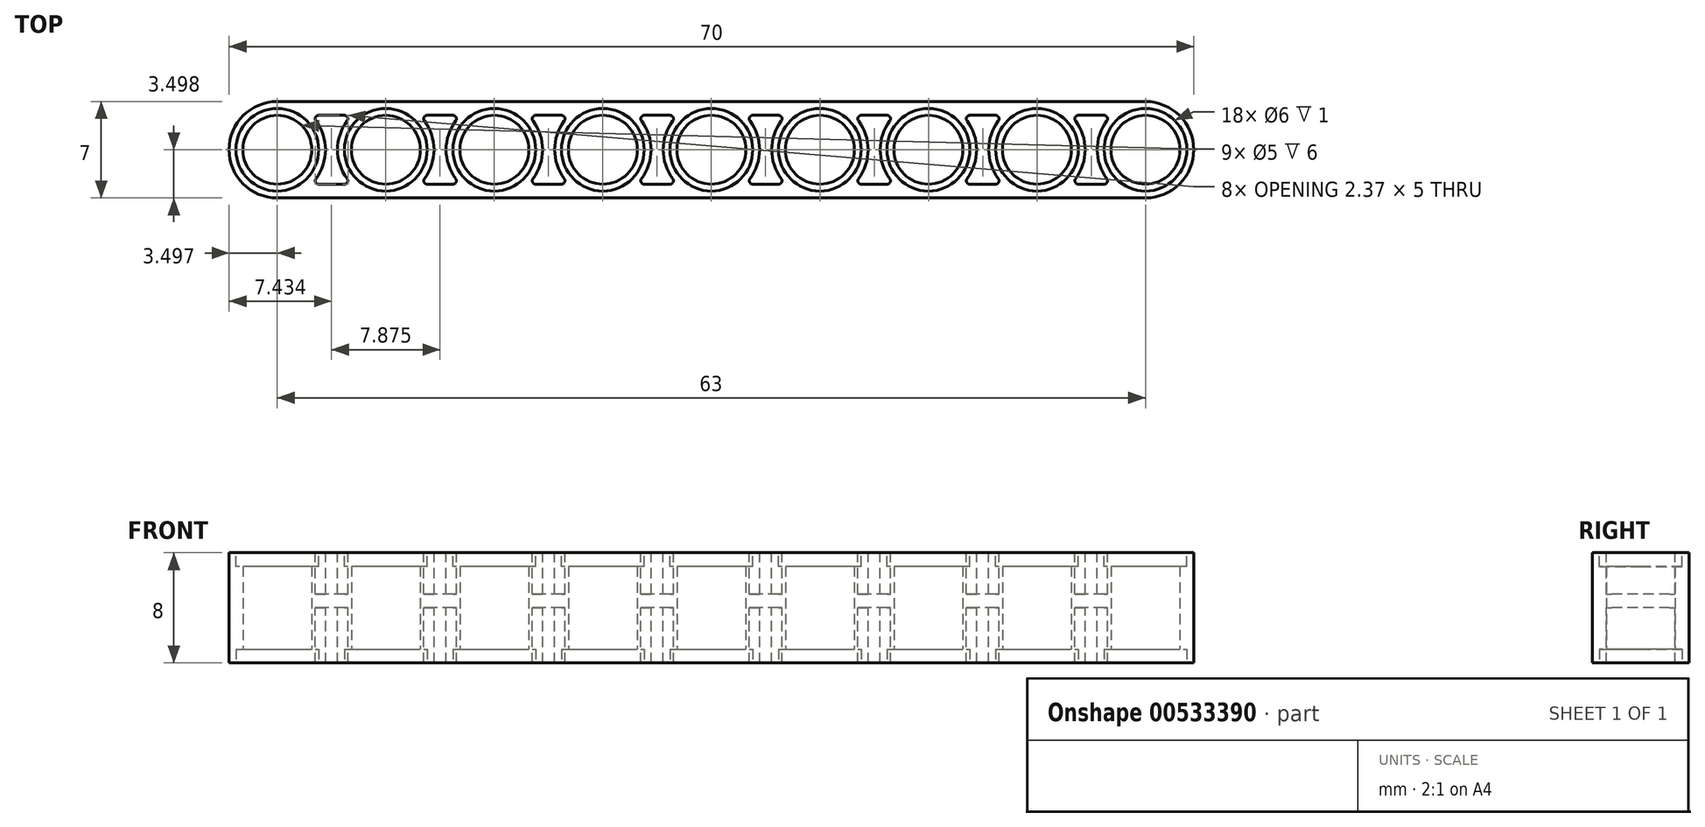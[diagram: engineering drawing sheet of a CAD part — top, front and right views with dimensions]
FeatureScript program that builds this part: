
annotation { "Feature Type Name" : "Feature", "Feature Type Description" : "" }
export const myFeature = defineFeature(function(context is Context, id is Id, definition is map)
    precondition{}
    {
        {
            var Q0;
            Q0=qCreatedBy(makeId("Top.planeOp"),FACE);
            var sketch = newSketch(context, id + "F0", { "sketchPlane" : qUnion([Q0])});
            skCircle(sketch, "E0", {"center": v(-40.67, -41.82) * mm, "radius": 3.5 * mm});
            skLineSegment(sketch, "E1", {"start": v(-40.67, -41.82) * mm, "end": v(22.33, -41.82) * mm});
            skCircle(sketch, "E2", {"center": v(22.33, -41.82) * mm, "radius": 3.5 * mm});
            skLineSegment(sketch, "E3", {"start": v(22.33, -45.32) * mm, "end": v(-40.67, -45.32) * mm});
            skLineSegment(sketch, "E4", {"start": v(-40.67, -38.32) * mm, "end": v(22.33, -38.32) * mm});
            skSolve(sketch);
        }
        {
            var Q0;
            Q0 = qSketchRegion(id + "F0", true);
            extrude(context, id + "F1", {"entities" : qUnion([Q0]), "depth" : 8 * mm, "offsetDistance" : 25 * mm});
        }
        {
            var Q0;
            Q0=makeQuery(id+"F1.opExtrude","CAP_FACE",FACE,{"disambiguationData":[OSD([sQuery(id+"F0.wireOp",EDGE,"E0"),sQuery(id+"F0.wireOp",EDGE,"E2"),sQuery(id+"F0.wireOp",EDGE,"E3"),sQuery(id+"F0.wireOp",EDGE,"E4")])],"isStart":true});
            var sketch = newSketch(context, id + "F2", { "sketchPlane" : qUnion([Q0])});
            skArc(sketch, "E5.0", {"start": v(-40.71, -42.4) * mm, "mid": v(-38.21, -39.9) * mm, "end": v(-40.71, -37.4) * mm});
            skArc(sketch, "E5.1", {"start": v(-40.71, -37.4) * mm, "mid": v(-43.21, -39.9) * mm, "end": v(-40.71, -42.4) * mm});
            skCircle(sketch, "E6.0", {"center": v(-40.71, -39.9) * mm, "radius": 3 * mm});
            skLineSegment(sketch, "E7", {"start": v(-38.26, -42.4) * mm, "end": v(-35.16, -42.4) * mm});
            skLineSegment(sketch, "E8", {"start": v(-38.26, -37.4) * mm, "end": v(-35.16, -37.4) * mm});
            skArc(sketch, "E9", {"start": v(-35.16, -37.4) * mm, "mid": v(-36.21, -39.9) * mm, "end": v(-35.16, -42.4) * mm});
            skArc(sketch, "E10", {"start": v(-38.26, -42.4) * mm, "mid": v(-37.21, -39.9) * mm, "end": v(-38.26, -37.4) * mm});
            skCircle(sketch, "E11", {"center": v(-40.67, 41.82) * mm, "radius": 3 * mm});
            skCircle(sketch, "E12", {"center": v(-40.67, 41.82) * mm, "radius": 2.5 * mm});
            skCircle(sketch, "E13.1.0.0", {"center": v(-32.8, 41.82) * mm, "radius": 2.5 * mm});
            skCircle(sketch, "E13.1.0.1", {"center": v(-32.8, 41.82) * mm, "radius": 3 * mm});
            skCircle(sketch, "E13.2.0.0", {"center": v(-24.92, 41.82) * mm, "radius": 2.5 * mm});
            skCircle(sketch, "E13.2.0.1", {"center": v(-24.92, 41.82) * mm, "radius": 3 * mm});
            skCircle(sketch, "E13.3.0.0", {"center": v(-17.05, 41.82) * mm, "radius": 2.5 * mm});
            skCircle(sketch, "E13.3.0.1", {"center": v(-17.05, 41.82) * mm, "radius": 3 * mm});
            skCircle(sketch, "E13.4.0.0", {"center": v(-9.17, 41.82) * mm, "radius": 2.5 * mm});
            skCircle(sketch, "E13.4.0.1", {"center": v(-9.17, 41.82) * mm, "radius": 3 * mm});
            skCircle(sketch, "E13.5.0.0", {"center": v(-1.3, 41.82) * mm, "radius": 2.5 * mm});
            skCircle(sketch, "E13.5.0.1", {"center": v(-1.3, 41.82) * mm, "radius": 3 * mm});
            skCircle(sketch, "E13.6.0.0", {"center": v(6.58, 41.82) * mm, "radius": 2.5 * mm});
            skCircle(sketch, "E13.6.0.1", {"center": v(6.58, 41.82) * mm, "radius": 3 * mm});
            skCircle(sketch, "E13.7.0.0", {"center": v(14.45, 41.82) * mm, "radius": 2.5 * mm});
            skCircle(sketch, "E13.7.0.1", {"center": v(14.45, 41.82) * mm, "radius": 3 * mm});
            skCircle(sketch, "E13.8.0.0", {"center": v(22.33, 41.82) * mm, "radius": 2.5 * mm});
            skCircle(sketch, "E13.8.0.1", {"center": v(22.33, 41.82) * mm, "radius": 3 * mm});
            skLineSegment(sketch, "E13.direction1", {"start": v(-40.67, 41.82) * mm, "end": v(-32.8, 41.82) * mm, "construction": true});
            skSolve(sketch);
        }
        {
            var Q0;
            Q0=makeQuery(id+"F2.imprint","IMPRINT",FACE,{"disambiguationData":[TD([[makeQuery(id+"F2.imprint","IMPRINT",EDGE,{"derivedFrom":sQuery(id+"F2.wireOp",EDGE,"E12")}),1.0]])]});
            var Q1;
            Q1=makeQuery(id+"F2.imprint","IMPRINT",FACE,{"disambiguationData":[TD([[makeQuery(id+"F2.imprint","IMPRINT",EDGE,{"derivedFrom":sQuery(id+"F2.wireOp",EDGE,"E13.1.0.0")}),1.0]])]});
            var Q2;
            Q2=makeQuery(id+"F2.imprint","IMPRINT",FACE,{"disambiguationData":[TD([[makeQuery(id+"F2.imprint","IMPRINT",EDGE,{"derivedFrom":sQuery(id+"F2.wireOp",EDGE,"E13.2.0.0")}),1.0]])]});
            var Q3;
            Q3=makeQuery(id+"F2.imprint","IMPRINT",FACE,{"disambiguationData":[TD([[makeQuery(id+"F2.imprint","IMPRINT",EDGE,{"derivedFrom":sQuery(id+"F2.wireOp",EDGE,"E13.3.0.0")}),1.0]])]});
            var Q4;
            Q4=makeQuery(id+"F2.imprint","IMPRINT",FACE,{"disambiguationData":[TD([[makeQuery(id+"F2.imprint","IMPRINT",EDGE,{"derivedFrom":sQuery(id+"F2.wireOp",EDGE,"E13.4.0.0")}),1.0]])]});
            var Q5;
            Q5=makeQuery(id+"F2.imprint","IMPRINT",FACE,{"disambiguationData":[TD([[makeQuery(id+"F2.imprint","IMPRINT",EDGE,{"derivedFrom":sQuery(id+"F2.wireOp",EDGE,"E13.5.0.0")}),1.0]])]});
            var Q6;
            Q6=makeQuery(id+"F2.imprint","IMPRINT",FACE,{"disambiguationData":[TD([[makeQuery(id+"F2.imprint","IMPRINT",EDGE,{"derivedFrom":sQuery(id+"F2.wireOp",EDGE,"E13.6.0.0")}),1.0]])]});
            var Q7;
            Q7=makeQuery(id+"F2.imprint","IMPRINT",FACE,{"disambiguationData":[TD([[makeQuery(id+"F2.imprint","IMPRINT",EDGE,{"derivedFrom":sQuery(id+"F2.wireOp",EDGE,"E13.7.0.0")}),1.0]])]});
            var Q8;
            Q8=makeQuery(id+"F2.imprint","IMPRINT",FACE,{"disambiguationData":[TD([[makeQuery(id+"F2.imprint","IMPRINT",EDGE,{"derivedFrom":sQuery(id+"F2.wireOp",EDGE,"E13.8.0.0")}),1.0]])]});
            extrude(context, id + "F3", {"entities" : qUnion([Q0, Q1, Q2, Q3, Q4, Q5, Q6, Q7, Q8]), "operationType" : NewBodyOperationType.REMOVE, "oppositeDirection" : true, "depth" : 25 * mm, "offsetDistance" : 25 * mm});
        }
        {
            var Q0;
            Q0=makeQuery(id+"F2.imprint","IMPRINT",FACE,{"disambiguationData":[TD([[makeQuery(id+"F2.imprint","IMPRINT",EDGE,{"derivedFrom":sQuery(id+"F2.wireOp",EDGE,"E11")}),1.0]])]});
            var Q1;
            Q1=makeQuery(id+"F2.imprint","IMPRINT",FACE,{"disambiguationData":[TD([[makeQuery(id+"F2.imprint","IMPRINT",EDGE,{"derivedFrom":sQuery(id+"F2.wireOp",EDGE,"E13.1.0.0")}),-1.0]])]});
            var Q2;
            Q2=makeQuery(id+"F2.imprint","IMPRINT",FACE,{"disambiguationData":[TD([[makeQuery(id+"F2.imprint","IMPRINT",EDGE,{"derivedFrom":sQuery(id+"F2.wireOp",EDGE,"E13.2.0.0")}),-1.0]])]});
            var Q3;
            Q3=makeQuery(id+"F2.imprint","IMPRINT",FACE,{"disambiguationData":[TD([[makeQuery(id+"F2.imprint","IMPRINT",EDGE,{"derivedFrom":sQuery(id+"F2.wireOp",EDGE,"E13.3.0.0")}),-1.0]])]});
            var Q4;
            Q4=makeQuery(id+"F2.imprint","IMPRINT",FACE,{"disambiguationData":[TD([[makeQuery(id+"F2.imprint","IMPRINT",EDGE,{"derivedFrom":sQuery(id+"F2.wireOp",EDGE,"E13.4.0.0")}),-1.0]])]});
            var Q5;
            Q5=makeQuery(id+"F2.imprint","IMPRINT",FACE,{"disambiguationData":[TD([[makeQuery(id+"F2.imprint","IMPRINT",EDGE,{"derivedFrom":sQuery(id+"F2.wireOp",EDGE,"E13.5.0.0")}),-1.0]])]});
            var Q6;
            Q6=makeQuery(id+"F2.imprint","IMPRINT",FACE,{"disambiguationData":[TD([[makeQuery(id+"F2.imprint","IMPRINT",EDGE,{"derivedFrom":sQuery(id+"F2.wireOp",EDGE,"E13.6.0.0")}),-1.0]])]});
            var Q7;
            Q7=makeQuery(id+"F2.imprint","IMPRINT",FACE,{"disambiguationData":[TD([[makeQuery(id+"F2.imprint","IMPRINT",EDGE,{"derivedFrom":sQuery(id+"F2.wireOp",EDGE,"E13.7.0.0")}),-1.0]])]});
            var Q8;
            Q8=makeQuery(id+"F2.imprint","IMPRINT",FACE,{"disambiguationData":[TD([[makeQuery(id+"F2.imprint","IMPRINT",EDGE,{"derivedFrom":sQuery(id+"F2.wireOp",EDGE,"E13.8.0.0")}),-1.0]])]});
            extrude(context, id + "F4", {"entities" : qUnion([Q0, Q1, Q2, Q3, Q4, Q5, Q6, Q7, Q8]), "operationType" : NewBodyOperationType.REMOVE, "oppositeDirection" : true, "depth" : 1 * mm, "offsetDistance" : 25 * mm});
        }
        {
            var Q0;
            Q0=makeQuery(id+"F1.opExtrude","CAP_FACE",FACE,{"disambiguationData":[OSD([sQuery(id+"F0.wireOp",EDGE,"E0"),sQuery(id+"F0.wireOp",EDGE,"E2"),sQuery(id+"F0.wireOp",EDGE,"E3"),sQuery(id+"F0.wireOp",EDGE,"E4")])],"isStart":false});
            var sketch = newSketch(context, id + "F5", { "sketchPlane" : qUnion([Q0])});
            skCircle(sketch, "E14", {"center": v(22.33, -41.82) * mm, "radius": 3 * mm});
            skCircle(sketch, "E15.1.0.0", {"center": v(14.45, -41.82) * mm, "radius": 3 * mm});
            skCircle(sketch, "E15.2.0.0", {"center": v(6.58, -41.82) * mm, "radius": 3 * mm});
            skCircle(sketch, "E15.3.0.0", {"center": v(-1.3, -41.82) * mm, "radius": 3 * mm});
            skCircle(sketch, "E15.4.0.0", {"center": v(-9.17, -41.82) * mm, "radius": 3 * mm});
            skCircle(sketch, "E15.5.0.0", {"center": v(-17.05, -41.82) * mm, "radius": 3 * mm});
            skCircle(sketch, "E15.6.0.0", {"center": v(-24.92, -41.82) * mm, "radius": 3 * mm});
            skCircle(sketch, "E15.7.0.0", {"center": v(-32.8, -41.82) * mm, "radius": 3 * mm});
            skCircle(sketch, "E15.8.0.0", {"center": v(-40.67, -41.82) * mm, "radius": 3 * mm});
            skLineSegment(sketch, "E15.direction1", {"start": v(22.33, -41.82) * mm, "end": v(14.45, -41.82) * mm, "construction": true});
            skSolve(sketch);
        }
        {
            var Q0;
            Q0=makeQuery(id+"F5.imprint","IMPRINT",FACE,{"disambiguationData":[TD([[makeQuery(id+"F5.imprint","IMPRINT",EDGE,{"derivedFrom":sQuery(id+"F5.wireOp",EDGE,"E14")}),1.0]])]});
            var Q1;
            Q1=makeQuery(id+"F5.imprint","IMPRINT",FACE,{"disambiguationData":[TD([[makeQuery(id+"F5.imprint","IMPRINT",EDGE,{"derivedFrom":sQuery(id+"F5.wireOp",EDGE,"E15.1.0.0")}),1.0]])]});
            var Q2;
            Q2=makeQuery(id+"F5.imprint","IMPRINT",FACE,{"disambiguationData":[TD([[makeQuery(id+"F5.imprint","IMPRINT",EDGE,{"derivedFrom":sQuery(id+"F5.wireOp",EDGE,"E15.2.0.0")}),1.0]])]});
            var Q3;
            Q3=makeQuery(id+"F5.imprint","IMPRINT",FACE,{"disambiguationData":[TD([[makeQuery(id+"F5.imprint","IMPRINT",EDGE,{"derivedFrom":sQuery(id+"F5.wireOp",EDGE,"E15.3.0.0")}),1.0]])]});
            var Q4;
            Q4=makeQuery(id+"F5.imprint","IMPRINT",FACE,{"disambiguationData":[TD([[makeQuery(id+"F5.imprint","IMPRINT",EDGE,{"derivedFrom":sQuery(id+"F5.wireOp",EDGE,"E15.4.0.0")}),1.0]])]});
            var Q5;
            Q5=makeQuery(id+"F5.imprint","IMPRINT",FACE,{"disambiguationData":[TD([[makeQuery(id+"F5.imprint","IMPRINT",EDGE,{"derivedFrom":sQuery(id+"F5.wireOp",EDGE,"E15.5.0.0")}),1.0]])]});
            var Q6;
            Q6=makeQuery(id+"F5.imprint","IMPRINT",FACE,{"disambiguationData":[TD([[makeQuery(id+"F5.imprint","IMPRINT",EDGE,{"derivedFrom":sQuery(id+"F5.wireOp",EDGE,"E15.6.0.0")}),1.0]])]});
            var Q7;
            Q7=makeQuery(id+"F5.imprint","IMPRINT",FACE,{"disambiguationData":[TD([[makeQuery(id+"F5.imprint","IMPRINT",EDGE,{"derivedFrom":sQuery(id+"F5.wireOp",EDGE,"E15.7.0.0")}),1.0]])]});
            var Q8;
            Q8=makeQuery(id+"F5.imprint","IMPRINT",FACE,{"disambiguationData":[TD([[makeQuery(id+"F5.imprint","IMPRINT",EDGE,{"derivedFrom":sQuery(id+"F5.wireOp",EDGE,"E15.8.0.0")}),1.0]])]});
            extrude(context, id + "F6", {"entities" : qUnion([Q0, Q1, Q2, Q3, Q4, Q5, Q6, Q7, Q8]), "operationType" : NewBodyOperationType.REMOVE, "oppositeDirection" : true, "depth" : 1 * mm, "offsetDistance" : 25 * mm});
        }
        {
            var Q0;
            Q0=makeQuery(id+"F1.opExtrude","CAP_FACE",FACE,{"disambiguationData":[OSD([sQuery(id+"F0.wireOp",EDGE,"E0"),sQuery(id+"F0.wireOp",EDGE,"E2"),sQuery(id+"F0.wireOp",EDGE,"E3"),sQuery(id+"F0.wireOp",EDGE,"E4")])],"isStart":false});
            var sketch = newSketch(context, id + "F7", { "sketchPlane" : qUnion([Q0])});
            skArc(sketch, "E16", {"start": v(19.52, -39.73) * mm, "mid": v(18.83, -41.82) * mm, "end": v(19.52, -43.92) * mm});
            skArc(sketch, "E17", {"start": v(17.25, -43.92) * mm, "mid": v(17.95, -41.82) * mm, "end": v(17.25, -39.73) * mm});
            skLineSegment(sketch, "E18", {"start": v(19.32, -44.32) * mm, "end": v(17.46, -44.32) * mm});
            skLineSegment(sketch, "E19", {"start": v(19.32, -39.32) * mm, "end": v(17.46, -39.32) * mm});
            skPoint(sketch, "E20.visualSharp", {"position": v(19.88, -44.32) * mm});
            skArc(sketch, "E20.filletArc", {"start": v(19.32, -44.32) * mm, "mid": v(19.55, -44.18) * mm, "end": v(19.52, -43.92) * mm});
            skPoint(sketch, "E21.visualSharp", {"position": v(16.9, -44.32) * mm});
            skArc(sketch, "E21.filletArc", {"start": v(17.25, -43.92) * mm, "mid": v(17.23, -44.18) * mm, "end": v(17.46, -44.32) * mm});
            skPoint(sketch, "E22.visualSharp", {"position": v(19.88, -39.32) * mm});
            skArc(sketch, "E22.filletArc", {"start": v(19.52, -39.73) * mm, "mid": v(19.55, -39.46) * mm, "end": v(19.32, -39.32) * mm});
            skPoint(sketch, "E23.visualSharp", {"position": v(16.9, -39.32) * mm});
            skArc(sketch, "E23.filletArc", {"start": v(17.46, -39.32) * mm, "mid": v(17.23, -39.46) * mm, "end": v(17.25, -39.73) * mm});
            skArc(sketch, "E24.1.0.0", {"start": v(11.65, -39.73) * mm, "mid": v(10.95, -41.82) * mm, "end": v(11.65, -43.92) * mm});
            skArc(sketch, "E24.1.0.1", {"start": v(9.38, -43.92) * mm, "mid": v(10.08, -41.82) * mm, "end": v(9.38, -39.73) * mm});
            skLineSegment(sketch, "E24.1.0.2", {"start": v(11.45, -44.32) * mm, "end": v(9.58, -44.32) * mm});
            skArc(sketch, "E24.1.0.3", {"start": v(11.45, -44.32) * mm, "mid": v(11.67, -44.18) * mm, "end": v(11.65, -43.92) * mm});
            skArc(sketch, "E24.1.0.4", {"start": v(9.38, -43.92) * mm, "mid": v(9.36, -44.18) * mm, "end": v(9.58, -44.32) * mm});
            skArc(sketch, "E24.1.0.5", {"start": v(9.58, -39.32) * mm, "mid": v(9.36, -39.46) * mm, "end": v(9.38, -39.73) * mm});
            skLineSegment(sketch, "E24.1.0.6", {"start": v(11.45, -39.32) * mm, "end": v(9.58, -39.32) * mm});
            skArc(sketch, "E24.1.0.7", {"start": v(11.65, -39.73) * mm, "mid": v(11.67, -39.46) * mm, "end": v(11.45, -39.32) * mm});
            skArc(sketch, "E24.2.0.0", {"start": v(3.77, -39.73) * mm, "mid": v(3.08, -41.82) * mm, "end": v(3.77, -43.92) * mm});
            skArc(sketch, "E24.2.0.1", {"start": v(1.5, -43.92) * mm, "mid": v(2.2, -41.82) * mm, "end": v(1.5, -39.73) * mm});
            skLineSegment(sketch, "E24.2.0.2", {"start": v(3.57, -44.32) * mm, "end": v(1.7, -44.32) * mm});
            skArc(sketch, "E24.2.0.3", {"start": v(3.57, -44.32) * mm, "mid": v(3.8, -44.18) * mm, "end": v(3.77, -43.92) * mm});
            skArc(sketch, "E24.2.0.4", {"start": v(1.5, -43.92) * mm, "mid": v(1.48, -44.18) * mm, "end": v(1.7, -44.32) * mm});
            skArc(sketch, "E24.2.0.5", {"start": v(1.7, -39.32) * mm, "mid": v(1.48, -39.46) * mm, "end": v(1.5, -39.73) * mm});
            skLineSegment(sketch, "E24.2.0.6", {"start": v(3.57, -39.32) * mm, "end": v(1.7, -39.32) * mm});
            skArc(sketch, "E24.2.0.7", {"start": v(3.77, -39.73) * mm, "mid": v(3.8, -39.46) * mm, "end": v(3.57, -39.32) * mm});
            skArc(sketch, "E24.3.0.0", {"start": v(-4.1, -39.73) * mm, "mid": v(-4.8, -41.82) * mm, "end": v(-4.1, -43.92) * mm});
            skArc(sketch, "E24.3.0.1", {"start": v(-6.37, -43.92) * mm, "mid": v(-5.67, -41.82) * mm, "end": v(-6.37, -39.73) * mm});
            skLineSegment(sketch, "E24.3.0.2", {"start": v(-4.3, -44.32) * mm, "end": v(-6.17, -44.32) * mm});
            skArc(sketch, "E24.3.0.3", {"start": v(-4.3, -44.32) * mm, "mid": v(-4.08, -44.18) * mm, "end": v(-4.1, -43.92) * mm});
            skArc(sketch, "E24.3.0.4", {"start": v(-6.37, -43.92) * mm, "mid": v(-6.4, -44.18) * mm, "end": v(-6.17, -44.32) * mm});
            skArc(sketch, "E24.3.0.5", {"start": v(-6.17, -39.32) * mm, "mid": v(-6.4, -39.46) * mm, "end": v(-6.37, -39.73) * mm});
            skLineSegment(sketch, "E24.3.0.6", {"start": v(-4.3, -39.32) * mm, "end": v(-6.17, -39.32) * mm});
            skArc(sketch, "E24.3.0.7", {"start": v(-4.1, -39.73) * mm, "mid": v(-4.08, -39.46) * mm, "end": v(-4.3, -39.32) * mm});
            skArc(sketch, "E24.4.0.0", {"start": v(-11.98, -39.73) * mm, "mid": v(-12.67, -41.82) * mm, "end": v(-11.98, -43.92) * mm});
            skArc(sketch, "E24.4.0.1", {"start": v(-14.25, -43.92) * mm, "mid": v(-13.55, -41.82) * mm, "end": v(-14.25, -39.73) * mm});
            skLineSegment(sketch, "E24.4.0.2", {"start": v(-12.18, -44.32) * mm, "end": v(-14.04, -44.32) * mm});
            skArc(sketch, "E24.4.0.3", {"start": v(-12.18, -44.32) * mm, "mid": v(-11.95, -44.18) * mm, "end": v(-11.98, -43.92) * mm});
            skArc(sketch, "E24.4.0.4", {"start": v(-14.25, -43.92) * mm, "mid": v(-14.27, -44.18) * mm, "end": v(-14.04, -44.32) * mm});
            skArc(sketch, "E24.4.0.5", {"start": v(-14.04, -39.32) * mm, "mid": v(-14.27, -39.46) * mm, "end": v(-14.25, -39.73) * mm});
            skLineSegment(sketch, "E24.4.0.6", {"start": v(-12.18, -39.32) * mm, "end": v(-14.04, -39.32) * mm});
            skArc(sketch, "E24.4.0.7", {"start": v(-11.98, -39.73) * mm, "mid": v(-11.95, -39.46) * mm, "end": v(-12.18, -39.32) * mm});
            skArc(sketch, "E24.5.0.0", {"start": v(-19.85, -39.73) * mm, "mid": v(-20.55, -41.82) * mm, "end": v(-19.85, -43.92) * mm});
            skArc(sketch, "E24.5.0.1", {"start": v(-22.12, -43.92) * mm, "mid": v(-21.42, -41.82) * mm, "end": v(-22.12, -39.73) * mm});
            skLineSegment(sketch, "E24.5.0.2", {"start": v(-20.05, -44.32) * mm, "end": v(-21.92, -44.32) * mm});
            skArc(sketch, "E24.5.0.3", {"start": v(-20.05, -44.32) * mm, "mid": v(-19.83, -44.18) * mm, "end": v(-19.85, -43.92) * mm});
            skArc(sketch, "E24.5.0.4", {"start": v(-22.12, -43.92) * mm, "mid": v(-22.14, -44.18) * mm, "end": v(-21.92, -44.32) * mm});
            skArc(sketch, "E24.5.0.5", {"start": v(-21.92, -39.32) * mm, "mid": v(-22.14, -39.46) * mm, "end": v(-22.12, -39.73) * mm});
            skLineSegment(sketch, "E24.5.0.6", {"start": v(-20.05, -39.32) * mm, "end": v(-21.92, -39.32) * mm});
            skArc(sketch, "E24.5.0.7", {"start": v(-19.85, -39.73) * mm, "mid": v(-19.83, -39.46) * mm, "end": v(-20.05, -39.32) * mm});
            skArc(sketch, "E24.6.0.0", {"start": v(-27.73, -39.73) * mm, "mid": v(-28.42, -41.82) * mm, "end": v(-27.73, -43.92) * mm});
            skArc(sketch, "E24.6.0.1", {"start": v(-30, -43.92) * mm, "mid": v(-29.3, -41.82) * mm, "end": v(-30, -39.73) * mm});
            skLineSegment(sketch, "E24.6.0.2", {"start": v(-27.93, -44.32) * mm, "end": v(-29.8, -44.32) * mm});
            skArc(sketch, "E24.6.0.3", {"start": v(-27.93, -44.32) * mm, "mid": v(-27.7, -44.18) * mm, "end": v(-27.73, -43.92) * mm});
            skArc(sketch, "E24.6.0.4", {"start": v(-30, -43.92) * mm, "mid": v(-30.02, -44.18) * mm, "end": v(-29.8, -44.32) * mm});
            skArc(sketch, "E24.6.0.5", {"start": v(-29.8, -39.32) * mm, "mid": v(-30.02, -39.46) * mm, "end": v(-30, -39.73) * mm});
            skLineSegment(sketch, "E24.6.0.6", {"start": v(-27.93, -39.32) * mm, "end": v(-29.8, -39.32) * mm});
            skArc(sketch, "E24.6.0.7", {"start": v(-27.73, -39.73) * mm, "mid": v(-27.7, -39.46) * mm, "end": v(-27.93, -39.32) * mm});
            skArc(sketch, "E24.7.0.0", {"start": v(-35.6, -39.73) * mm, "mid": v(-36.3, -41.82) * mm, "end": v(-35.6, -43.92) * mm});
            skArc(sketch, "E24.7.0.1", {"start": v(-37.87, -43.92) * mm, "mid": v(-37.17, -41.82) * mm, "end": v(-37.87, -39.73) * mm});
            skLineSegment(sketch, "E24.7.0.2", {"start": v(-35.8, -44.32) * mm, "end": v(-37.67, -44.32) * mm});
            skArc(sketch, "E24.7.0.3", {"start": v(-35.8, -44.32) * mm, "mid": v(-35.58, -44.18) * mm, "end": v(-35.6, -43.92) * mm});
            skArc(sketch, "E24.7.0.4", {"start": v(-37.87, -43.92) * mm, "mid": v(-37.9, -44.18) * mm, "end": v(-37.67, -44.32) * mm});
            skArc(sketch, "E24.7.0.5", {"start": v(-37.67, -39.32) * mm, "mid": v(-37.9, -39.46) * mm, "end": v(-37.87, -39.73) * mm});
            skLineSegment(sketch, "E24.7.0.6", {"start": v(-35.8, -39.32) * mm, "end": v(-37.67, -39.32) * mm});
            skArc(sketch, "E24.7.0.7", {"start": v(-35.6, -39.73) * mm, "mid": v(-35.58, -39.46) * mm, "end": v(-35.8, -39.32) * mm});
            skLineSegment(sketch, "E24.direction1", {"start": v(14.45, -41.82) * mm, "end": v(6.58, -41.82) * mm, "construction": true});
            skSolve(sketch);
        }
        {
            var Q0;
            Q0=makeQuery(id+"F7.imprint","IMPRINT",FACE,{"disambiguationData":[TD([[makeQuery(id+"F7.imprint","IMPRINT",EDGE,{"derivedFrom":sQuery(id+"F7.wireOp",EDGE,"E16")}),-1.0]])]});
            var Q1;
            Q1=makeQuery(id+"F7.imprint","IMPRINT",FACE,{"disambiguationData":[TD([[makeQuery(id+"F7.imprint","IMPRINT",EDGE,{"derivedFrom":sQuery(id+"F7.wireOp",EDGE,"E24.1.0.0")}),-1.0]])]});
            var Q2;
            Q2=makeQuery(id+"F7.imprint","IMPRINT",FACE,{"disambiguationData":[TD([[makeQuery(id+"F7.imprint","IMPRINT",EDGE,{"derivedFrom":sQuery(id+"F7.wireOp",EDGE,"E24.2.0.0")}),-1.0]])]});
            var Q3;
            Q3=makeQuery(id+"F7.imprint","IMPRINT",FACE,{"disambiguationData":[TD([[makeQuery(id+"F7.imprint","IMPRINT",EDGE,{"derivedFrom":sQuery(id+"F7.wireOp",EDGE,"E24.3.0.0")}),-1.0]])]});
            var Q4;
            Q4=makeQuery(id+"F7.imprint","IMPRINT",FACE,{"disambiguationData":[TD([[makeQuery(id+"F7.imprint","IMPRINT",EDGE,{"derivedFrom":sQuery(id+"F7.wireOp",EDGE,"E24.4.0.0")}),-1.0]])]});
            var Q5;
            Q5=makeQuery(id+"F7.imprint","IMPRINT",FACE,{"disambiguationData":[TD([[makeQuery(id+"F7.imprint","IMPRINT",EDGE,{"derivedFrom":sQuery(id+"F7.wireOp",EDGE,"E24.5.0.0")}),-1.0]])]});
            var Q6;
            Q6=makeQuery(id+"F7.imprint","IMPRINT",FACE,{"disambiguationData":[TD([[makeQuery(id+"F7.imprint","IMPRINT",EDGE,{"derivedFrom":sQuery(id+"F7.wireOp",EDGE,"E24.7.0.0")}),-1.0]])]});
            var Q7;
            Q7=makeQuery(id+"F7.imprint","IMPRINT",FACE,{"disambiguationData":[TD([[makeQuery(id+"F7.imprint","IMPRINT",EDGE,{"derivedFrom":sQuery(id+"F7.wireOp",EDGE,"E24.6.0.0")}),-1.0]])]});
            extrude(context, id + "F8", {"entities" : qUnion([Q0, Q1, Q2, Q3, Q4, Q5, Q6, Q7]), "operationType" : NewBodyOperationType.REMOVE, "oppositeDirection" : true, "depth" : 8 * mm, "offsetDistance" : 25 * mm});
        }
        {
            var Q0;
            Q0 = qSketchRegion(id + "F7", true);
            extrude(context, id + "F9", {"entities" : qUnion([Q0]), "operationType" : NewBodyOperationType.ADD, "oppositeDirection" : true, "depth" : 4 * mm, "offsetDistance" : 25 * mm});
        }
        {
            var Q0;
            Q0 = qSketchRegion(id + "F7", true);
            extrude(context, id + "F10", {"entities" : qUnion([Q0]), "operationType" : NewBodyOperationType.REMOVE, "oppositeDirection" : true, "depth" : 3 * mm, "offsetDistance" : 25 * mm});
        }
    });
